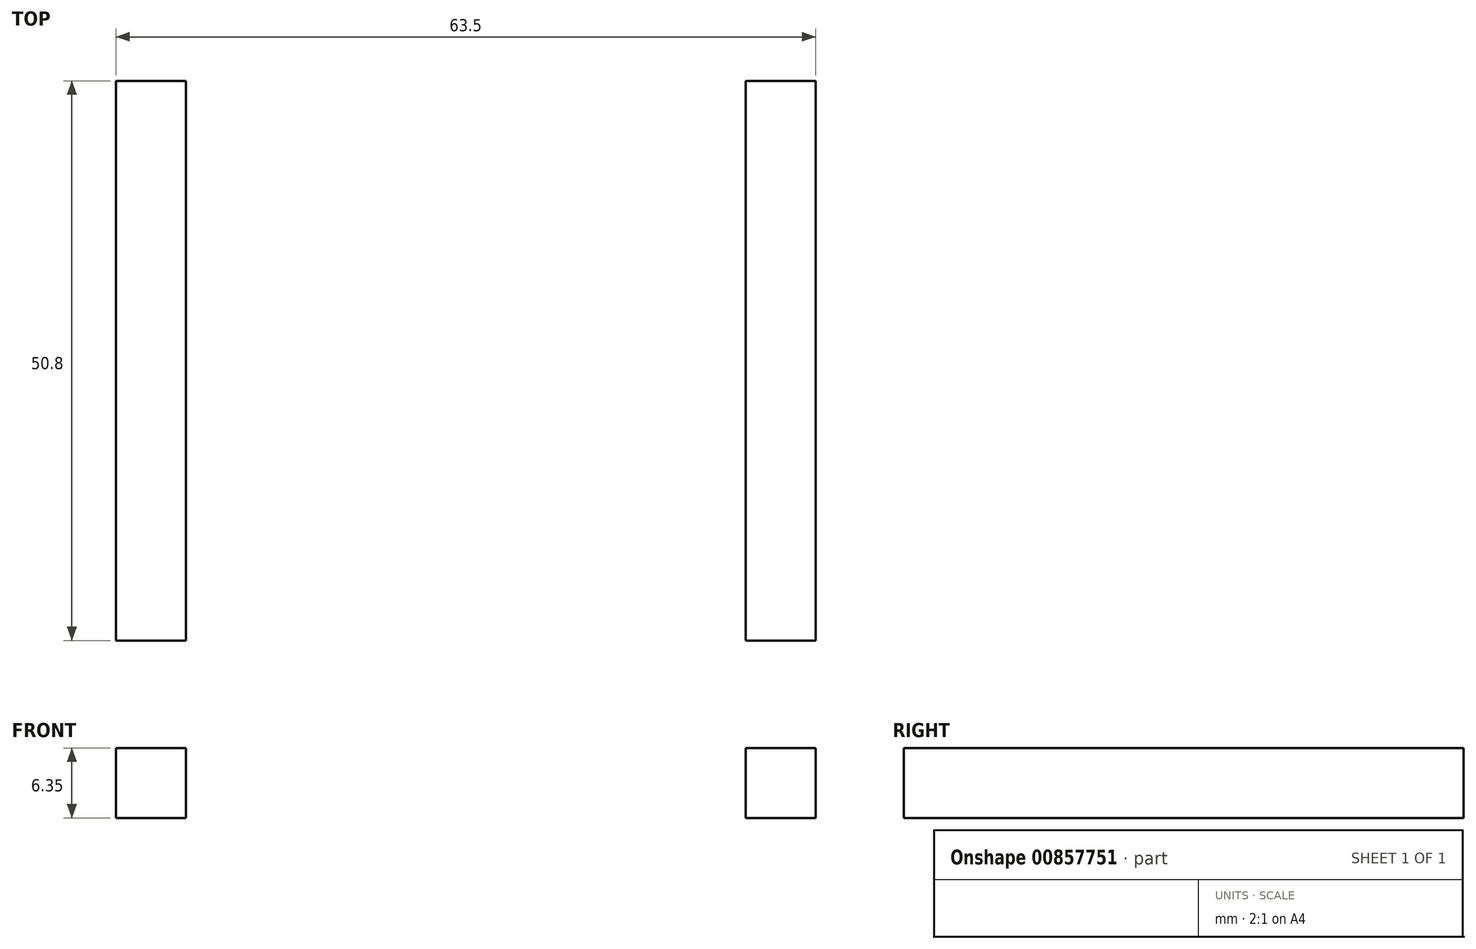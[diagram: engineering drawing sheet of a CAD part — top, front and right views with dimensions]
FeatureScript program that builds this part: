
annotation { "Feature Type Name" : "Feature", "Feature Type Description" : "" }
export const myFeature = defineFeature(function(context is Context, id is Id, definition is map)
    precondition{}
    {
        {
            var Q0;
            Q0=qCreatedBy(makeId("Top.planeOp"),FACE);
            var sketch = newSketch(context, id + "F0", { "sketchPlane" : qUnion([Q0])});
            skLineSegment(sketch, "E0", {"start": v(0, 0) * mm, "end": v(50.8, 0) * mm});
            skLineSegment(sketch, "E1.bottom", {"start": v(0, 0) * mm, "end": v(-6.35, 0) * mm});
            skLineSegment(sketch, "E1.top", {"start": v(0, -50.8) * mm, "end": v(-6.35, -50.8) * mm});
            skLineSegment(sketch, "E1.left", {"start": v(0, 0) * mm, "end": v(0, -50.8) * mm});
            skLineSegment(sketch, "E1.right", {"start": v(-6.35, 0) * mm, "end": v(-6.35, -50.8) * mm});
            skLineSegment(sketch, "E2.bottom", {"start": v(50.8, 0) * mm, "end": v(57.15, 0) * mm});
            skLineSegment(sketch, "E2.top", {"start": v(50.8, -50.8) * mm, "end": v(57.15, -50.8) * mm});
            skLineSegment(sketch, "E2.left", {"start": v(50.8, 0) * mm, "end": v(50.8, -50.8) * mm});
            skLineSegment(sketch, "E2.right", {"start": v(57.15, 0) * mm, "end": v(57.15, -50.8) * mm});
            skSolve(sketch);
        }
        {
            var Q0;
            Q0=qSketchRegion(id+"F0",true);
            extrude(context, id + "F1", {"entities" : qUnion([Q0]), "depth" : 6.35 * mm, "offsetDistance" : 25.4 * mm});
        }
    });
